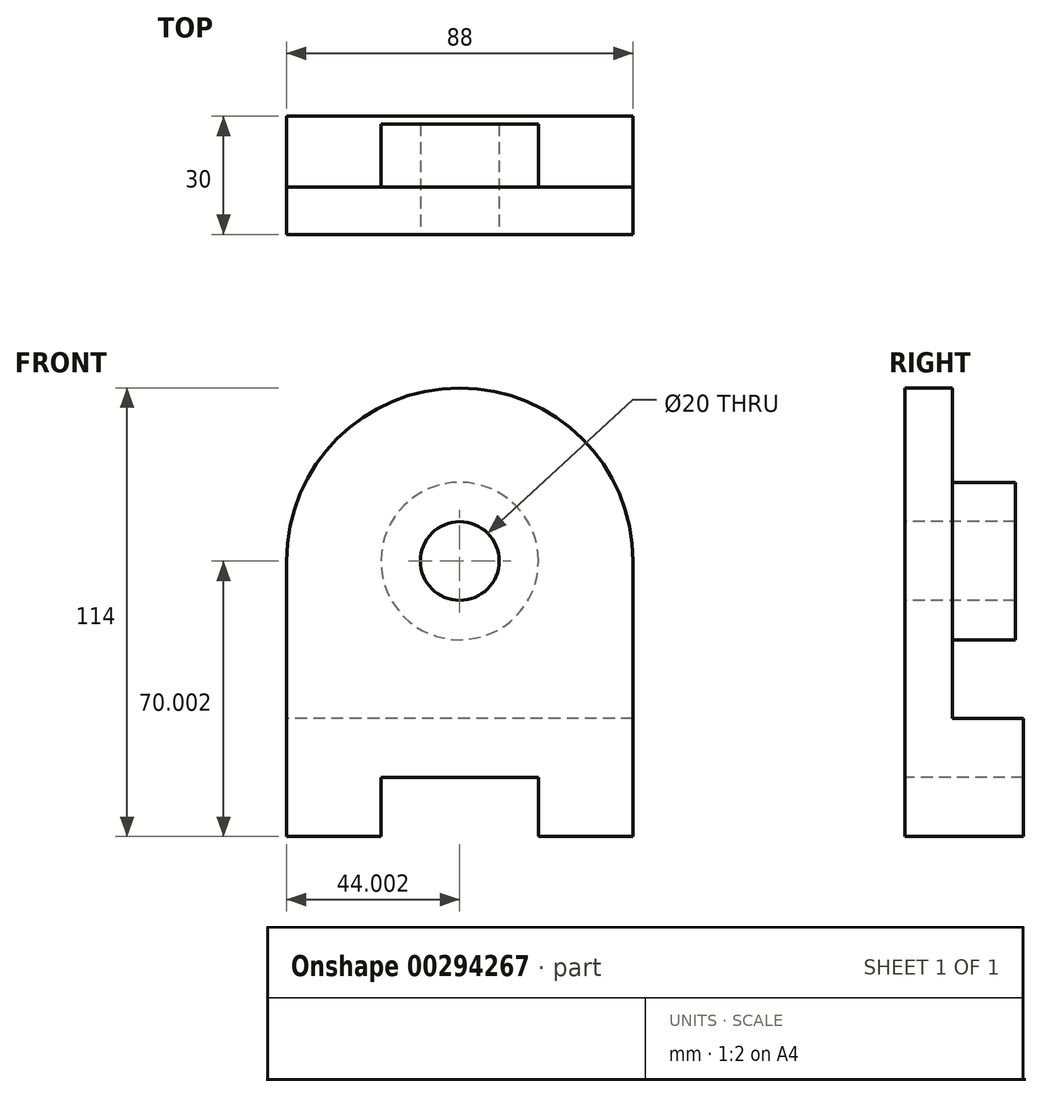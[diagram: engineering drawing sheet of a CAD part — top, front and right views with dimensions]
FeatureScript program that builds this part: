
annotation { "Feature Type Name" : "Feature", "Feature Type Description" : "" }
export const myFeature = defineFeature(function(context is Context, id is Id, definition is map)
    precondition{}
    {
        {
            var Q0;
            Q0=qCreatedBy(makeId("Front.planeOp"),FACE);
            var sketch = newSketch(context, id + "F0", { "sketchPlane" : qUnion([Q0])});
            skLineSegment(sketch, "E0", {"start": v(-36.5, 47.95) * mm, "end": v(-36.5, -29.02) * mm, "construction": true});
            skLineSegment(sketch, "E1", {"start": v(-91.52, 10.98) * mm, "end": v(-3.93, 10.98) * mm, "construction": true});
            skArc(sketch, "E2", {"start": v(-36.5, 54.98) * mm, "mid": v(-67.61, 42.1) * mm, "end": v(-80.5, 10.98) * mm});
            skArc(sketch, "E3", {"start": v(-36.5, 30.98) * mm, "mid": v(-56.5, 10.98) * mm, "end": v(-36.5, -9.02) * mm});
            skArc(sketch, "E4", {"start": v(-36.5, 20.98) * mm, "mid": v(-46.5, 10.98) * mm, "end": v(-36.5, 0.98) * mm});
            skLineSegment(sketch, "E5", {"start": v(-80.5, 10.98) * mm, "end": v(-80.5, -59.02) * mm});
            skLineSegment(sketch, "E6", {"start": v(-80.5, -59.02) * mm, "end": v(-56.5, -59.02) * mm});
            skLineSegment(sketch, "E7", {"start": v(-56.5, -59.02) * mm, "end": v(-56.5, -44.02) * mm});
            skLineSegment(sketch, "E8", {"start": v(-56.5, -44.02) * mm, "end": v(-36.5, -44.02) * mm});
            skLineSegment(sketch, "E9", {"start": v(-36.5, -44.02) * mm, "end": v(-36.5, -29.02) * mm, "construction": true});
            skLineSegment(sketch, "E10", {"start": v(-36.5, -29.02) * mm, "end": v(-80.5, -29.02) * mm});
            skArc(sketch, "E11.MirrorCS", {"start": v(-36.5, 54.98) * mm, "mid": v(-5.39, 42.1) * mm, "end": v(7.5, 10.98) * mm});
            skLineSegment(sketch, "E12.MirrorCS", {"start": v(7.5, 10.98) * mm, "end": v(7.5, -59.02) * mm});
            skLineSegment(sketch, "E13.MirrorCS", {"start": v(7.5, -59.02) * mm, "end": v(-16.5, -59.02) * mm});
            skLineSegment(sketch, "E14.MirrorCS", {"start": v(-16.5, -59.02) * mm, "end": v(-16.5, -44.02) * mm});
            skLineSegment(sketch, "E15.MirrorCS", {"start": v(-16.5, -44.02) * mm, "end": v(-36.5, -44.02) * mm});
            skLineSegment(sketch, "E16.MirrorCS", {"start": v(-36.5, -29.02) * mm, "end": v(7.5, -29.02) * mm});
            skArc(sketch, "E17.MirrorCS", {"start": v(-36.5, 20.98) * mm, "mid": v(-26.5, 10.98) * mm, "end": v(-36.5, 0.98) * mm});
            skArc(sketch, "E18.MirrorCS", {"start": v(-36.5, 30.98) * mm, "mid": v(-16.5, 10.98) * mm, "end": v(-36.5, -9.02) * mm});
            skLineSegment(sketch, "E19", {"start": v(-3.93, 10.98) * mm, "end": v(7.5, 10.98) * mm, "construction": true});
            skLineSegment(sketch, "E20", {"start": v(-36.5, 47.95) * mm, "end": v(-36.5, 54.98) * mm, "construction": true});
            skPoint(sketch, "E21.orphan", {"position": v(-36.5, -33.02) * mm});
            skSolve(sketch);
        }
        {
            var Q0;
            {var subQ0=sQuery(id+"F0.wireOp",EDGE,"E6");Q0=makeQuery(id+"F0.imprint","IMPRINT",FACE,{"disambiguationData":[TD([[makeQuery(id+"F0.imprint","IMPRINT",EDGE,{"derivedFrom":subQ0}),1.0]])]});}
            extrude(context, id + "F1", {"entities" : qUnion([Q0]), "oppositeDirection" : true, "depth" : 30 * mm});
        }
        {
            var Q0;
            {var subQ2=sQuery(id+"F0.wireOp",EDGE,"E2");Q0=makeQuery(id+"F0.imprint","IMPRINT",FACE,{"disambiguationData":[TD([[makeQuery(id+"F0.imprint","IMPRINT",EDGE,{"derivedFrom":subQ2}),1.0]])]});}
            extrude(context, id + "F2", {"entities" : qUnion([Q0]), "operationType" : NewBodyOperationType.ADD, "oppositeDirection" : true, "depth" : 12 * mm});
        }
        {
            var Q0;
            Q0=makeQuery(id+"F0.imprint","IMPRINT",FACE,{"disambiguationData":[TD([[makeQuery(id+"F0.imprint","IMPRINT",EDGE,{"derivedFrom":sQuery(id+"F0.wireOp",EDGE,"E3")}),1.0]])]});
            extrude(context, id + "F3", {"entities" : qUnion([Q0]), "operationType" : NewBodyOperationType.ADD, "oppositeDirection" : true, "depth" : 28 * mm});
        }
    });
